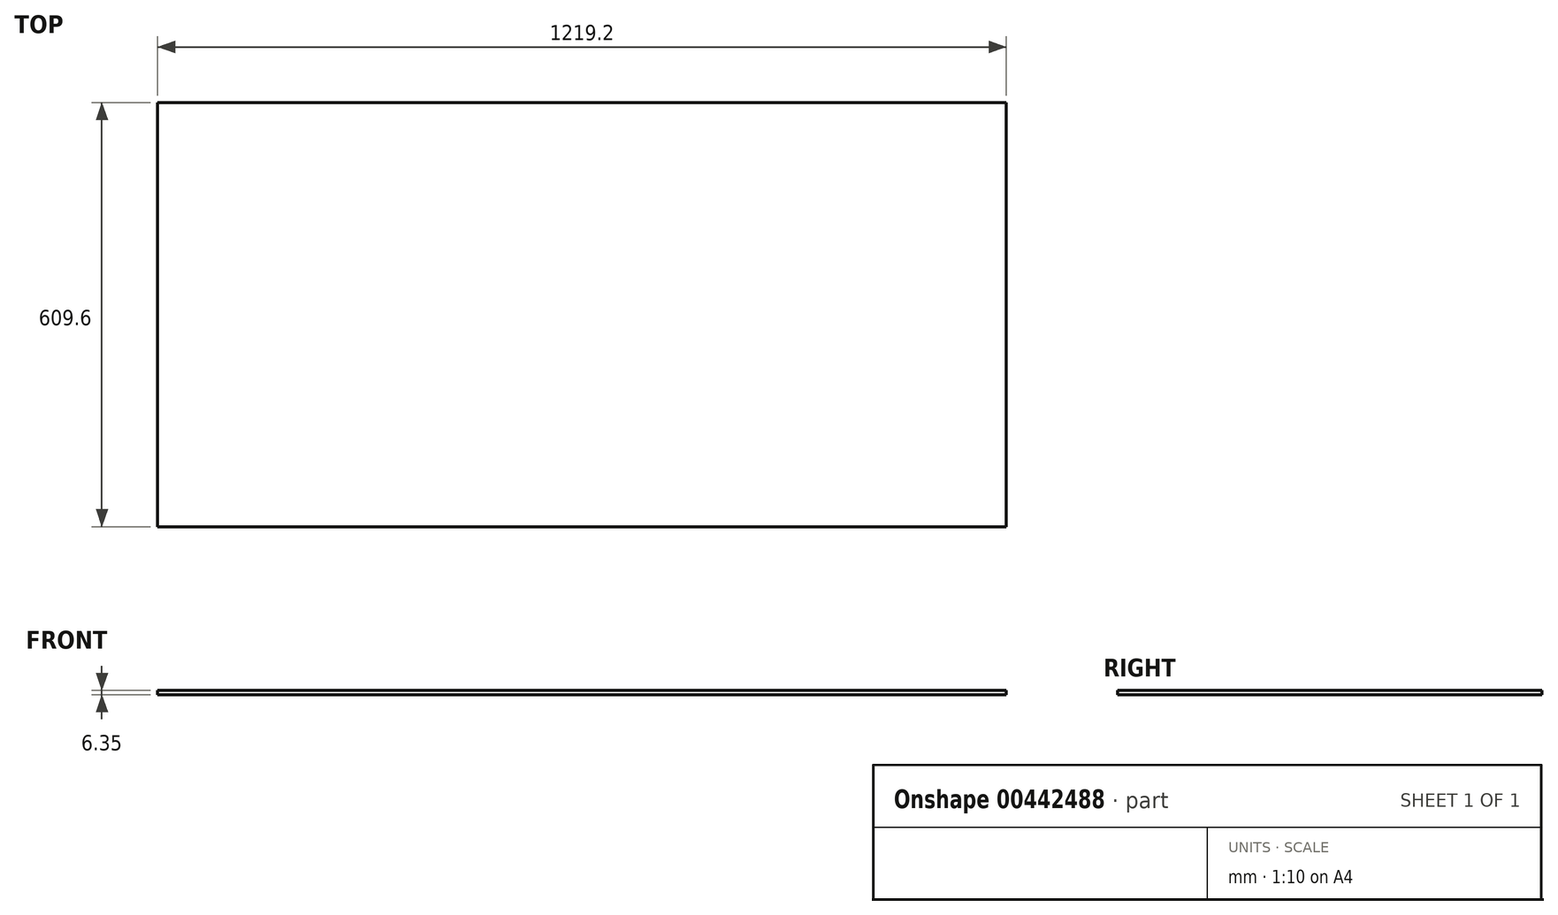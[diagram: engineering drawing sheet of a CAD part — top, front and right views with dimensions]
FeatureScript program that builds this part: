
annotation { "Feature Type Name" : "Feature", "Feature Type Description" : "" }
export const myFeature = defineFeature(function(context is Context, id is Id, definition is map)
    precondition{}
    {
        {
            var Q0;
            Q0=qCreatedBy(makeId("Top.planeOp"),FACE);
            var sketch = newSketch(context, id + "F0", { "sketchPlane" : qUnion([Q0])});
            skLineSegment(sketch, "E0.bottom", {"start": v(0, 0) * mm, "end": v(1219.2, 0) * mm});
            skLineSegment(sketch, "E0.top", {"start": v(0, -609.6) * mm, "end": v(1219.2, -609.6) * mm});
            skLineSegment(sketch, "E0.left", {"start": v(0, 0) * mm, "end": v(0, -609.6) * mm});
            skLineSegment(sketch, "E0.right", {"start": v(1219.2, 0) * mm, "end": v(1219.2, -609.6) * mm});
            skSolve(sketch);
        }
        {
            var Q0;
            Q0=makeQuery(id+"F0.imprint","IMPRINT",FACE,{"disambiguationData":[TD([[makeQuery(id+"F0.imprint","IMPRINT",EDGE,{"derivedFrom":sQuery(id+"F0.wireOp",EDGE,"E0.bottom")}),-1.0]])]});
            extrude(context, id + "F1", {"entities" : qUnion([Q0]), "depth" : 6.35 * mm});
        }
    });
